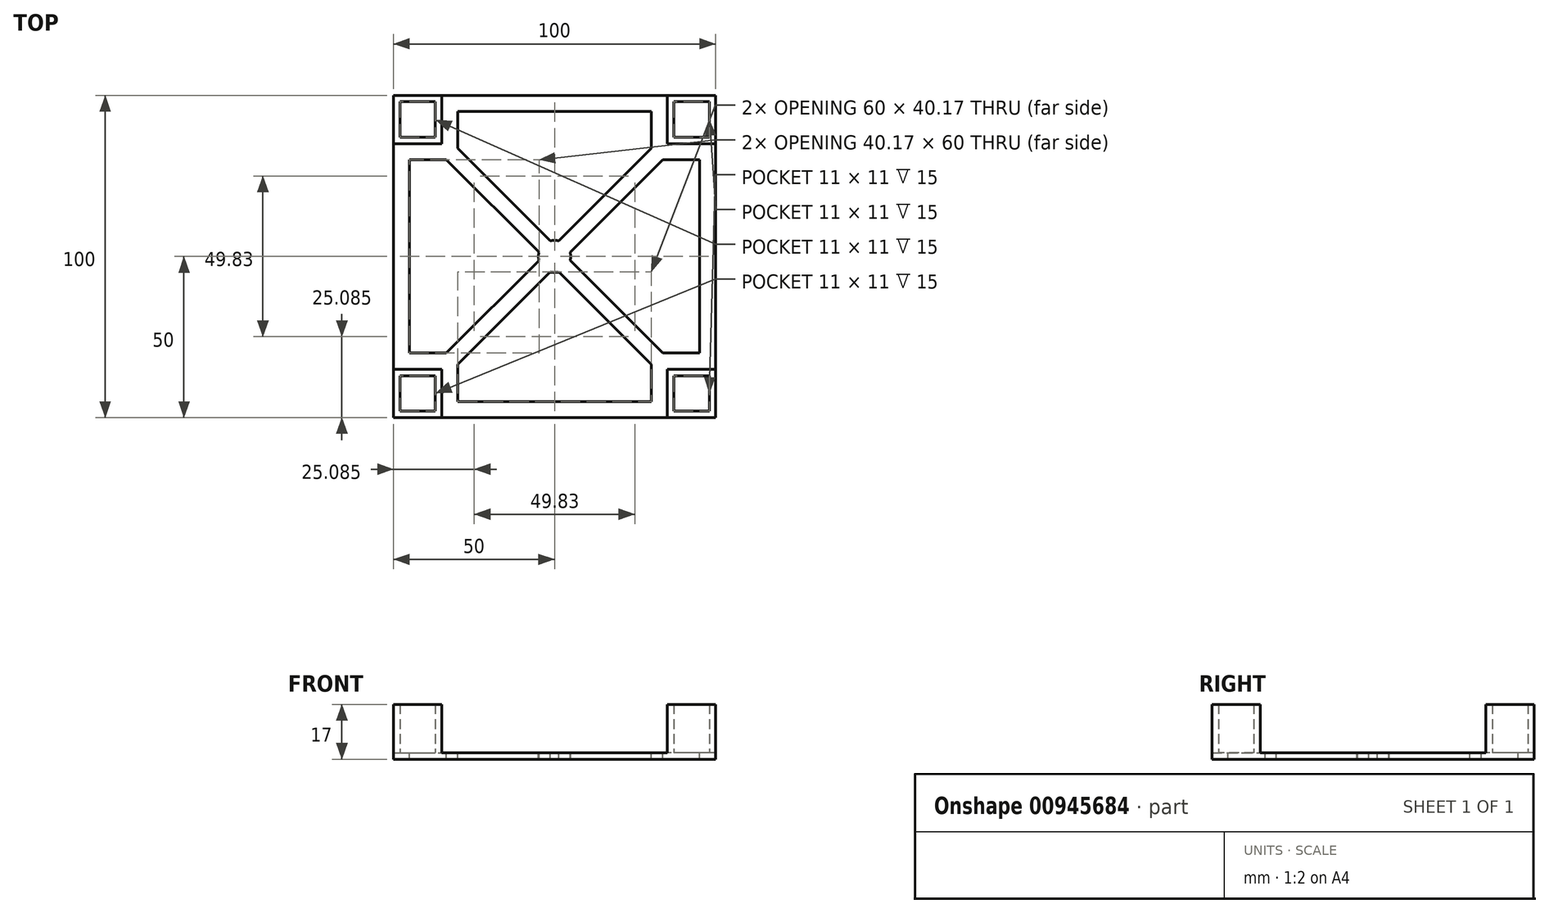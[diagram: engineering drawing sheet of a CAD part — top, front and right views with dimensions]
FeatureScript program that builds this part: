
annotation { "Feature Type Name" : "Feature", "Feature Type Description" : "" }
export const myFeature = defineFeature(function(context is Context, id is Id, definition is map)
    precondition{}
    {
        {
            var Q0;
            Q0=qCreatedBy(makeId("Top.planeOp"),FACE);
            var sketch = newSketch(context, id + "F0", { "sketchPlane" : qUnion([Q0])});
            skLineSegment(sketch, "E0.bottom", {"start": v(50, 50) * mm, "end": v(-50, 50) * mm});
            skLineSegment(sketch, "E0.top", {"start": v(50, -50) * mm, "end": v(-50, -50) * mm});
            skLineSegment(sketch, "E0.left", {"start": v(50, 50) * mm, "end": v(50, -50) * mm});
            skLineSegment(sketch, "E0.right", {"start": v(-50, 50) * mm, "end": v(-50, -50) * mm});
            skPoint(sketch, "E0.middle", {"position": v(0, 0) * mm});
            skSolve(sketch);
        }
        {
            var Q0;
            Q0 = qSketchRegion(id + "F0", true);
            extrude(context, id + "F1", {"entities" : qUnion([Q0]), "depth" : 2 * mm, "offsetDistance" : 25 * mm});
        }
        {
            var Q0;
            Q0=makeQuery(id+"F1.opExtrude","CAP_FACE",FACE,{"disambiguationData":[OSD([sQuery(id+"F0.wireOp",EDGE,"E0.bottom"),sQuery(id+"F0.wireOp",EDGE,"E0.top"),sQuery(id+"F0.wireOp",EDGE,"E0.left"),sQuery(id+"F0.wireOp",EDGE,"E0.right")])],"isStart":false});
            var sketch = newSketch(context, id + "F2", { "sketchPlane" : qUnion([Q0])});
            skLineSegment(sketch, "E1.bottom", {"start": v(-50, -50) * mm, "end": v(-35, -50) * mm});
            skLineSegment(sketch, "E1.top", {"start": v(-50, -35) * mm, "end": v(-35, -35) * mm});
            skLineSegment(sketch, "E1.left", {"start": v(-50, -50) * mm, "end": v(-50, -35) * mm});
            skLineSegment(sketch, "E1.right", {"start": v(-35, -50) * mm, "end": v(-35, -35) * mm});
            skLineSegment(sketch, "E2.bottom", {"start": v(-50, 50) * mm, "end": v(-35, 50) * mm});
            skLineSegment(sketch, "E2.top", {"start": v(-50, 35) * mm, "end": v(-35, 35) * mm});
            skLineSegment(sketch, "E2.left", {"start": v(-50, 50) * mm, "end": v(-50, 35) * mm});
            skLineSegment(sketch, "E2.right", {"start": v(-35, 50) * mm, "end": v(-35, 35) * mm});
            skLineSegment(sketch, "E3.bottom", {"start": v(50, 50) * mm, "end": v(35, 50) * mm});
            skLineSegment(sketch, "E3.top", {"start": v(50, 35) * mm, "end": v(35, 35) * mm});
            skLineSegment(sketch, "E3.left", {"start": v(50, 50) * mm, "end": v(50, 35) * mm});
            skLineSegment(sketch, "E3.right", {"start": v(35, 50) * mm, "end": v(35, 35) * mm});
            skLineSegment(sketch, "E4.bottom", {"start": v(50, -50) * mm, "end": v(35, -50) * mm});
            skLineSegment(sketch, "E4.top", {"start": v(50, -35) * mm, "end": v(35, -35) * mm});
            skLineSegment(sketch, "E4.left", {"start": v(50, -50) * mm, "end": v(50, -35) * mm});
            skLineSegment(sketch, "E4.right", {"start": v(35, -50) * mm, "end": v(35, -35) * mm});
            skSolve(sketch);
        }
        {
            var Q0;
            Q0 = qSketchRegion(id + "F2", true);
            extrude(context, id + "F3", {"entities" : qUnion([Q0]), "operationType" : NewBodyOperationType.ADD, "depth" : 15 * mm, "offsetDistance" : 25 * mm});
        }
        {
            var Q0;
            Q0=makeQuery(id+"F3.opExtrude","CAP_FACE",FACE,{"disambiguationData":[OSD([sQuery(id+"F2.wireOp",EDGE,"E2.bottom"),sQuery(id+"F2.wireOp",EDGE,"E2.top"),sQuery(id+"F2.wireOp",EDGE,"E2.left"),sQuery(id+"F2.wireOp",EDGE,"E2.right")])],"isStart":false});
            var Q1;
            Q1=makeQuery(id+"F3.opExtrude","CAP_FACE",FACE,{"disambiguationData":[OSD([sQuery(id+"F2.wireOp",EDGE,"E4.bottom"),sQuery(id+"F2.wireOp",EDGE,"E4.top"),sQuery(id+"F2.wireOp",EDGE,"E4.left"),sQuery(id+"F2.wireOp",EDGE,"E4.right")])],"isStart":false});
            var Q2;
            Q2=makeQuery(id+"F3.opExtrude","CAP_FACE",FACE,{"disambiguationData":[OSD([sQuery(id+"F2.wireOp",EDGE,"E1.bottom"),sQuery(id+"F2.wireOp",EDGE,"E1.top"),sQuery(id+"F2.wireOp",EDGE,"E1.left"),sQuery(id+"F2.wireOp",EDGE,"E1.right")])],"isStart":false});
            var Q3;
            Q3=makeQuery(id+"F3.opExtrude","CAP_FACE",FACE,{"disambiguationData":[OSD([sQuery(id+"F2.wireOp",EDGE,"E3.bottom"),sQuery(id+"F2.wireOp",EDGE,"E3.top"),sQuery(id+"F2.wireOp",EDGE,"E3.left"),sQuery(id+"F2.wireOp",EDGE,"E3.right")])],"isStart":false});
            shell(context, id + "F4", {"entities" : qUnion([Q0, Q1, Q2, Q3]), "thickness" : 2 * mm});
        }
        {
            var Q0;
            Q0=makeQuery(id+"F1.opExtrude","CAP_FACE",FACE,{"disambiguationData":[OSD([sQuery(id+"F0.wireOp",EDGE,"E0.bottom"),sQuery(id+"F0.wireOp",EDGE,"E0.top"),sQuery(id+"F0.wireOp",EDGE,"E0.left"),sQuery(id+"F0.wireOp",EDGE,"E0.right")])],"isStart":false});
            var sketch = newSketch(context, id + "F5", { "sketchPlane" : qUnion([Q0])});
            skLineSegment(sketch, "E5.0", {"start": v(30, -45) * mm, "end": v(30, -33.54) * mm});
            skLineSegment(sketch, "E5.1", {"start": v(-45, 30) * mm, "end": v(-33.54, 30) * mm});
            skLineSegment(sketch, "E5.2", {"start": v(-45, 30) * mm, "end": v(-45, -30) * mm});
            skLineSegment(sketch, "E5.3", {"start": v(-45, -30) * mm, "end": v(-33.54, -30) * mm});
            skLineSegment(sketch, "E5.4", {"start": v(-30, -45) * mm, "end": v(-30, -33.54) * mm});
            skLineSegment(sketch, "E5.5", {"start": v(-30, 45) * mm, "end": v(-30, 33.54) * mm});
            skLineSegment(sketch, "E5.6", {"start": v(30, -45) * mm, "end": v(-30, -45) * mm});
            skLineSegment(sketch, "E5.7", {"start": v(30, 45) * mm, "end": v(-30, 45) * mm});
            skLineSegment(sketch, "E5.8", {"start": v(30, 45) * mm, "end": v(30, 33.54) * mm});
            skLineSegment(sketch, "E5.9", {"start": v(45, 30) * mm, "end": v(33.54, 30) * mm});
            skLineSegment(sketch, "E5.10", {"start": v(45, 30) * mm, "end": v(45, -30) * mm});
            skLineSegment(sketch, "E5.11", {"start": v(45, -30) * mm, "end": v(33.54, -30) * mm});
            skArc(sketch, "E6", {"start": v(-4.83, 1.3) * mm, "mid": v(-5, 0) * mm, "end": v(-4.83, -1.3) * mm});
            skLineSegment(sketch, "E7", {"start": v(-30, -30) * mm, "end": v(30, 30) * mm, "construction": true});
            skLineSegment(sketch, "E8", {"start": v(30, -30) * mm, "end": v(-30, 30) * mm, "construction": true});
            skLineSegment(sketch, "E9.0", {"start": v(-30, -33.54) * mm, "end": v(-1.3, -4.83) * mm});
            skLineSegment(sketch, "E10.MirrorCS", {"start": v(-33.54, -30) * mm, "end": v(-4.83, -1.3) * mm});
            skLineSegment(sketch, "E11.MirrorCS", {"start": v(-30, 30) * mm, "end": v(30, -30) * mm, "construction": true});
            skLineSegment(sketch, "E12.0", {"start": v(33.54, -30) * mm, "end": v(4.83, -1.3) * mm});
            skLineSegment(sketch, "E13.MirrorCS", {"start": v(30, -33.54) * mm, "end": v(1.3, -4.83) * mm});
            skArc(sketch, "E14.trimOffspring", {"start": v(-1.3, -4.83) * mm, "mid": v(0, -5) * mm, "end": v(1.3, -4.83) * mm});
            skArc(sketch, "E15.trimOffspring", {"start": v(4.83, -1.3) * mm, "mid": v(5, 0) * mm, "end": v(4.83, 1.3) * mm});
            skArc(sketch, "E16.trimOffspring", {"start": v(1.3, 4.83) * mm, "mid": v(0, 5) * mm, "end": v(-1.3, 4.83) * mm});
            skLineSegment(sketch, "E17.trimOffspring", {"start": v(1.3, 4.83) * mm, "end": v(30, 33.54) * mm});
            skLineSegment(sketch, "E18.trimOffspring", {"start": v(-1.3, 4.83) * mm, "end": v(-30, 33.54) * mm});
            skLineSegment(sketch, "E19.trimOffspring", {"start": v(-4.83, 1.3) * mm, "end": v(-33.54, 30) * mm});
            skLineSegment(sketch, "E20.trimOffspring", {"start": v(4.83, 1.3) * mm, "end": v(33.54, 30) * mm});
            skPoint(sketch, "E21.orphan", {"position": v(-28.23, 31.77) * mm});
            skPoint(sketch, "E22.orphan", {"position": v(-31.77, 28.23) * mm});
            skPoint(sketch, "E23.orphan", {"position": v(28.23, 31.77) * mm});
            skPoint(sketch, "E24.orphan", {"position": v(31.77, 28.23) * mm});
            skPoint(sketch, "E25.orphan", {"position": v(31.77, -28.23) * mm});
            skPoint(sketch, "E26.orphan", {"position": v(28.23, -31.77) * mm});
            skPoint(sketch, "E27.orphan", {"position": v(-28.23, -31.77) * mm});
            skPoint(sketch, "E28.orphan", {"position": v(-31.77, -28.23) * mm});
            skSolve(sketch);
        }
        {
            var Q0;
            Q0 = qSketchRegion(id + "F5", true);
            extrude(context, id + "F6", {"entities" : qUnion([Q0]), "operationType" : NewBodyOperationType.REMOVE, "endBound" : BoundingType.THROUGH_ALL, "oppositeDirection" : true, "depth" : 25 * mm, "offsetDistance" : 25 * mm});
        }
    });
